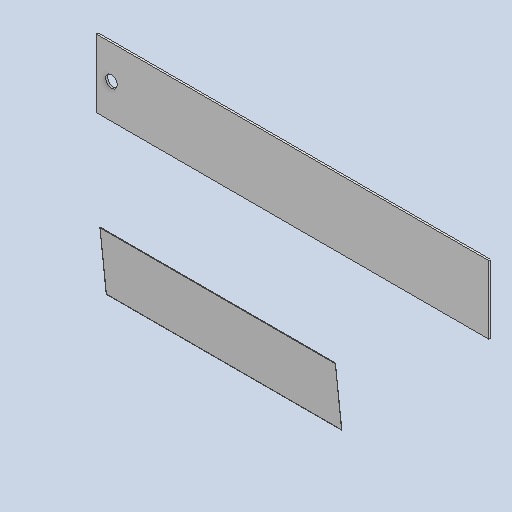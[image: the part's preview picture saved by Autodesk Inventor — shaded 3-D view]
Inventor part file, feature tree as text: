
AUTODESK INVENTOR PART (.ipt)
format: ipt  version: 2023 (Build 270158000, 158)  size: 190,976 bytes
history: native  units: in
note: dims shown in document units (in); Inventor stores cm internally (conversion verified against a paired STEP export)
features: other x9, reference x7, extrude x5, sketch x5, projected_geometry x3
ambient origin geometry x8: Origin, YZ Plane, XZ Plane, XY Plane, X Axis, Y Axis, Z Axis, Center Point
bodies: Body1 (feature_tree)
feature tree (29):
  other  "Bryła1"
  extrude  "Wyciągnięcie proste1"  Depth=0.1181in
  sketch  "Szkic2"
  other  "Płaszczyzna konstrukcyjna1"
  extrude  "Wyciągnięcie proste2"  Depth=2.3622in
  extrude  "Wyciągnięcie proste3"  Depth=0.7874in
  extrude  "Wyciągnięcie proste4"  Depth=0.0197in TaperAngle=0.0deg
  extrude  "Wyciągnięcie proste5"  Depth=0.0197in TaperAngle=0.0deg
  sketch  "Szkic1"
  reference  "Odniesienie1"
  reference  "Odniesienie2"
  reference  "Odniesienie3"
  projected_geometry  "Pętla rzutowana1"
  sketch  "Szkic3"
  projected_geometry  "Pętla rzutowana2"
  reference  "Odniesienie4"
  reference  "Odniesienie5"
  sketch  "Szkic4"
  projected_geometry  "Pętla rzutowana3"
  sketch  "Szkic5"
  reference  "Odniesienie6"
  reference  "Odniesienie7"
  other  "<userpath>\Desktop\MojeRoboty\Stefan\mechanics 2\STEFAN.iam"
  other  "STEFAN.iam"
  other  "sciana_prawa_nowa_MIR:1"
  other  "sciana_prawa_nowa:1"
  other  "dach:1"
  other  "uchwyt_silnikow:1"
  other  "podstawa:1"
